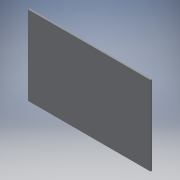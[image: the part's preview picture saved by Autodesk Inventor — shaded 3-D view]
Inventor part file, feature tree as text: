
AUTODESK INVENTOR PART (.ipt)
format: ipt  version: 2016 (Build 200138000, 138)  size: 83,456 bytes
history: native  units: in
note: dims shown in document units (in); Inventor stores cm internally (conversion verified against a paired STEP export)
features: extrude x1, sketch x1
ambient origin geometry x8: Origin, YZ Plane, XZ Plane, XY Plane, X Axis, Y Axis, Z Axis, Center Point
bodies: Solid1 (feature_tree)
feature tree (2):
  extrude  "Extrusion1"  Depth=2.1654in
  sketch  "Sketch1"  dims[d0=3.3465in d1=2.1654in d2=0.0394in d3=0.0in]
